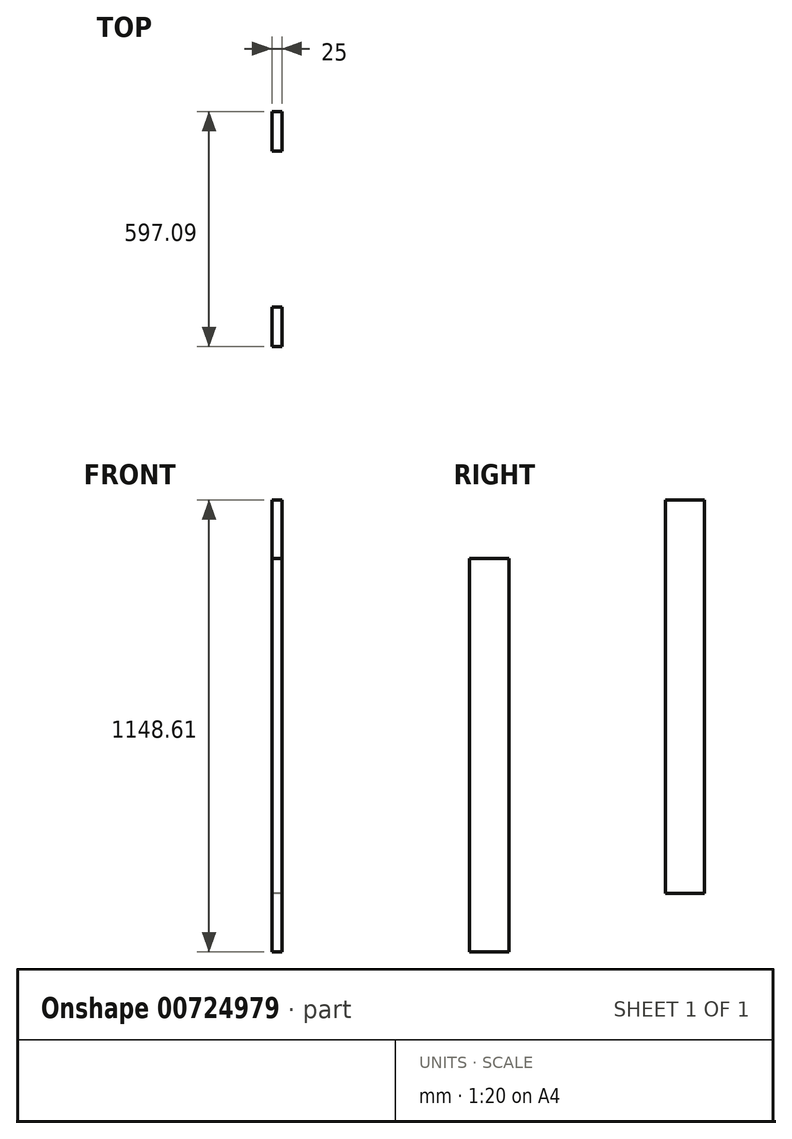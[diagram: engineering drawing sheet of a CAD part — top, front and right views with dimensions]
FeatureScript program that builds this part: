
annotation { "Feature Type Name" : "Feature", "Feature Type Description" : "" }
export const myFeature = defineFeature(function(context is Context, id is Id, definition is map)
    precondition{}
    {
        {
            var Q0;
            Q0=qCreatedBy(makeId("Right.planeOp"),FACE);
            var sketch = newSketch(context, id + "F0", { "sketchPlane" : qUnion([Q0])});
            skLineSegment(sketch, "E0.bottom", {"start": v(-32.79, 1011.47) * mm, "end": v(67.21, 1011.47) * mm});
            skLineSegment(sketch, "E0.top", {"start": v(-32.79, 11.47) * mm, "end": v(67.21, 11.47) * mm});
            skLineSegment(sketch, "E0.left", {"start": v(-32.79, 1011.47) * mm, "end": v(-32.79, 11.47) * mm});
            skLineSegment(sketch, "E0.right", {"start": v(67.21, 1011.47) * mm, "end": v(67.21, 11.47) * mm});
            skLineSegment(sketch, "E1.bottom", {"start": v(-529.88, 862.86) * mm, "end": v(-429.88, 862.86) * mm});
            skLineSegment(sketch, "E1.top", {"start": v(-529.88, -137.14) * mm, "end": v(-429.88, -137.14) * mm});
            skLineSegment(sketch, "E1.left", {"start": v(-529.88, 862.86) * mm, "end": v(-529.88, -137.14) * mm});
            skLineSegment(sketch, "E1.right", {"start": v(-429.88, 862.86) * mm, "end": v(-429.88, -137.14) * mm});
            skSolve(sketch);
        }
        {
            var Q0;
            Q0=makeQuery(id+"F0.imprint","IMPRINT",FACE,{"disambiguationData":[TD([[makeQuery(id+"F0.imprint","IMPRINT",EDGE,{"derivedFrom":sQuery(id+"F0.wireOp",EDGE,"E0.bottom")}),-1.0]])]});
            var Q1;
            Q1=makeQuery(id+"F0.imprint","IMPRINT",FACE,{"disambiguationData":[TD([[makeQuery(id+"F0.imprint","IMPRINT",EDGE,{"derivedFrom":sQuery(id+"F0.wireOp",EDGE,"E1.bottom")}),-1.0]])]});
            extrude(context, id + "F1", {"entities" : qUnion([Q0, Q1]), "depth" : 25 * mm, "offsetDistance" : 25 * mm});
        }
    });
